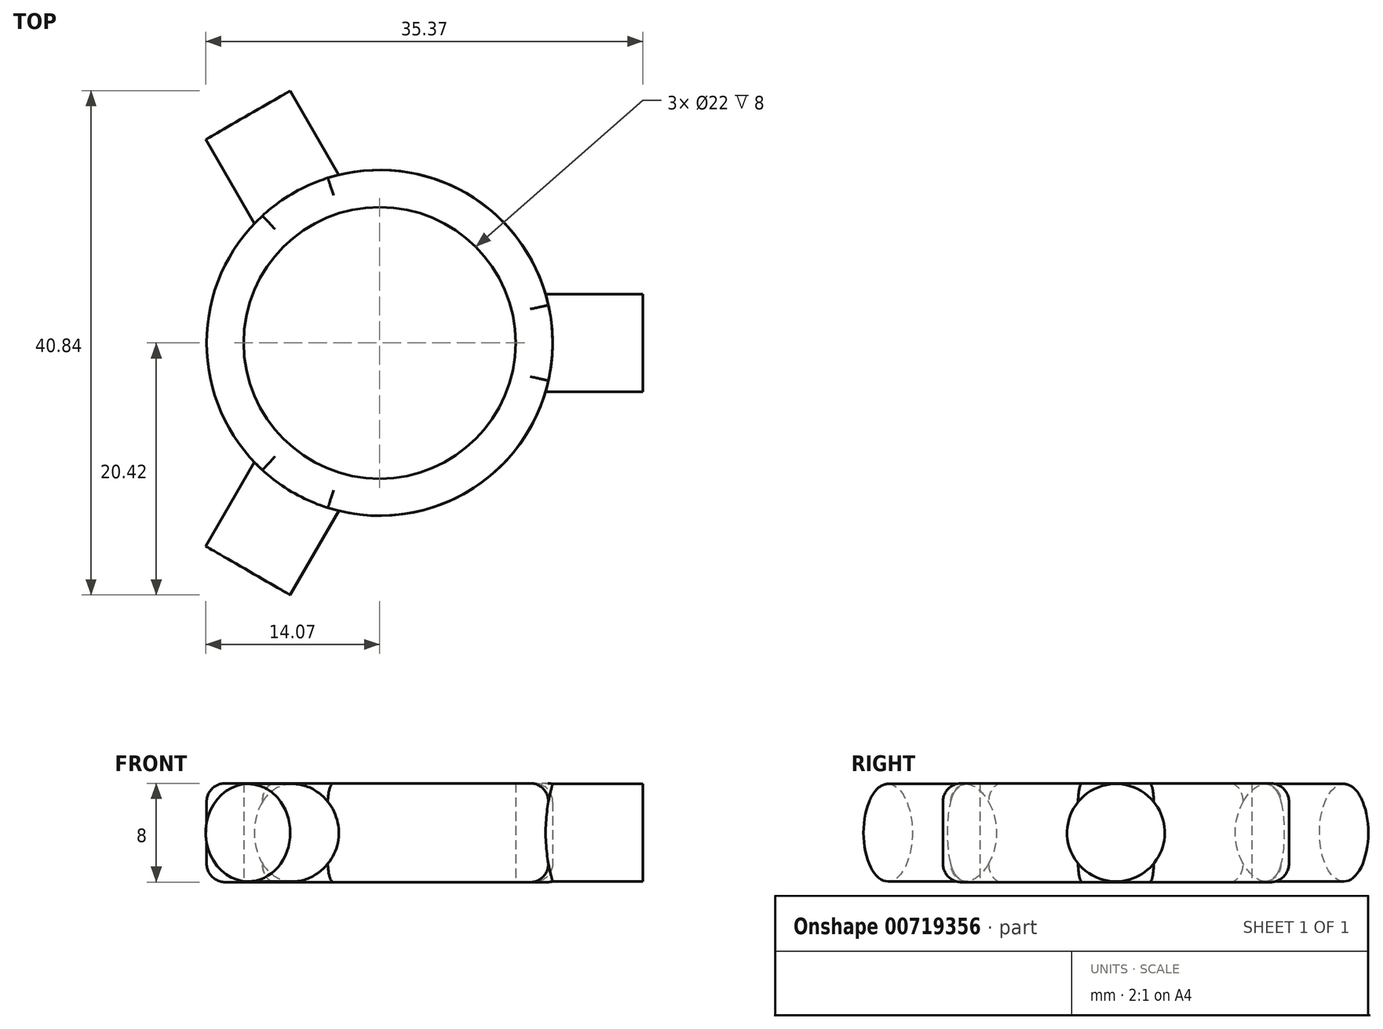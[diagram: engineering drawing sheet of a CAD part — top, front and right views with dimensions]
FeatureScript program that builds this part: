
annotation { "Feature Type Name" : "Feature", "Feature Type Description" : "" }
export const myFeature = defineFeature(function(context is Context, id is Id, definition is map)
    precondition{}
    {
        {
            var Q0;
            Q0=qCreatedBy(makeId("Top.planeOp"),FACE);
            var sketch = newSketch(context, id + "F0", { "sketchPlane" : qUnion([Q0])});
            skCircle(sketch, "E0", {"center": v(0, 0) * mm, "radius": 11 * mm});
            skCircle(sketch, "E1.0", {"center": v(0, 0) * mm, "radius": 14 * mm});
            skSolve(sketch);
        }
        {
            var Q0;
            Q0=qCreatedBy(makeId("Right.planeOp"),FACE);
            cPlane(context, id + "F1", {"entities" : qUnion([Q0]), "cplaneType" : CPlaneType.OFFSET, "offset" : 13.3 * mm, "width" : 150 * mm, "height" : 150 * mm});
        }
        {
            var Q0;
            Q0=qCreatedBy(id+"F1.planeOp",FACE);
            var sketch = newSketch(context, id + "F2", { "sketchPlane" : qUnion([Q0])});
            skCircle(sketch, "E2", {"center": v(0, 0) * mm, "radius": 3.95 * mm});
            skSolve(sketch);
        }
        {
            var Q0;
            Q0=makeQuery(id+"F0.imprint","IMPRINT",FACE,{"disambiguationData":[TD([[makeQuery(id+"F0.imprint","IMPRINT",EDGE,{"derivedFrom":sQuery(id+"F0.wireOp",EDGE,"E0")}),-1.0]])]});
            extrude(context, id + "F3", {"entities" : qUnion([Q0]), "endBound" : BoundingType.SYMMETRIC, "depth" : 8 * mm, "offsetDistance" : 25 * mm});
        }
        {
            var Q0;
            Q0 = qSketchRegion(id + "F2", true);
            extrude(context, id + "F4", {"entities" : qUnion([Q0]), "operationType" : NewBodyOperationType.ADD, "depth" : 8 * mm, "offsetDistance" : 25 * mm});
        }
        {
            var Q0;
            Q0=makeQuery(id+"F3.opExtrude","CAP_EDGE",EDGE,{"disambiguationData":[OSD([sQuery(id+"F0.wireOp",EDGE,"E1.0")])],"isStart":false});
            var Q1;
            Q1=makeQuery(id+"F3.opExtrude","CAP_EDGE",EDGE,{"disambiguationData":[OSD([sQuery(id+"F0.wireOp",EDGE,"E1.0")])],"isStart":true});
            fillet(context, id + "F5", {"entities" : qUnion([Q0, Q1]), "radius" : 1.5 * mm, "tangentPropagation" : true, "allowEdgeOverflow" : false});
        }
        {
            var Q0;
            Q0=makeQuery(id+"F3.opExtrude","SWEPT_BODY",BODY,{"disambiguationData":[OSD([sQuery(id+"F0.wireOp",EDGE,"E0"),sQuery(id+"F0.wireOp",EDGE,"E1.0")])]});
            var Q1;
            Q1=makeQuery(id+"F3.opExtrude","CAP_EDGE",EDGE,{"disambiguationData":[OSD([sQuery(id+"F0.wireOp",EDGE,"E0")])],"isStart":false});
            circularPattern(context, id + "F6", {"entities" : qUnion([Q0]), "axis" : qUnion([Q1]), "angle" : 360 * degree, "instanceCount" : 3, "equalSpace" : true});
        }
    });
